# Revit family: Haworth_Very_Chair_WireStacker
name_source: partatom
category: Furniture
revit_build: Autodesk Revit 2018 (Build: 20170223_1515(x64)
units: mm (PartAtom-declared; Revit-internal decimal feet)

## family parameters
Always vertical = Yes
Cut with Voids When Loaded = No
OmniClass Number = 23.40.70.14.64.21
OmniClass Title = Systems Furniture
Room Calculation Point = No
Shared = No
Work Plane-Based = No

## types (2) — shared parameters
Actual Depth = 23 1/4"
Actual Width = 21 3/4"
Arm Cap Finish = Haworth _ Polymer _ Slate
Assembly Code = E2020200
Cushion Finish = Haworth _ Fabric _ Tellure _ Sky 3A-32
Description = Wire Stacking Chair
Frame Finish = Haworth _ Metal _ Chrome
Manufacturer = Haworth
Model = Haworth - Chair - Very
Revision Number = 7
Seat Finish = Haworth _ Polymer _ Slate
Size = Verify Final Dim. w/ Haworth
Sustainability Info = https://www.haworth.com
URL = www.haworth.com
URL - Product = http://www.haworth.com
Warranty = http://www.haworth.com
With Arms = No
With Back Cushion = Yes
With Seat Cushion = Yes

## per-type parameters (varying)
| type | Actual Height | Chair | Stool |
| Stool | 41 9/16" | No | Yes |
| Chair | 30 9/16" | Yes | No |

## geometry (parser evidence)
native form markers: Sweep x13
no freeform markers — native parametric forms only
